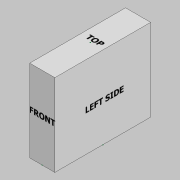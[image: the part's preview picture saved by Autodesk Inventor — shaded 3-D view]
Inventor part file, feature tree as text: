
AUTODESK INVENTOR PART (.ipt)
format: ipt  version: 2021 (Build 250183000, 183)  size: 95,232 bytes
history: native  units: mm
features: sketch x7, extrude x1
ambient origin geometry x8: Origin, YZ Plane, XZ Plane, XY Plane, X Axis, Y Axis, Z Axis, Center Point
bodies: Solid1 (feature_tree)
feature tree (8):
  extrude  "Extrusion1"  Depth=106.7mm
  sketch  "Sketch2"  dims[d2=53.35mm]
  sketch  "Sketch3"  dims[d3=14.0mm]
  sketch  "Sketch4"  dims[d4=91.4mm]
  sketch  "Sketch5"  dims[d5=0.0mm]
  sketch  "Sketch6"
  sketch  "Sketch7"
  sketch  "Sketch1"  dims[d0=28.0mm d1=106.7mm]
